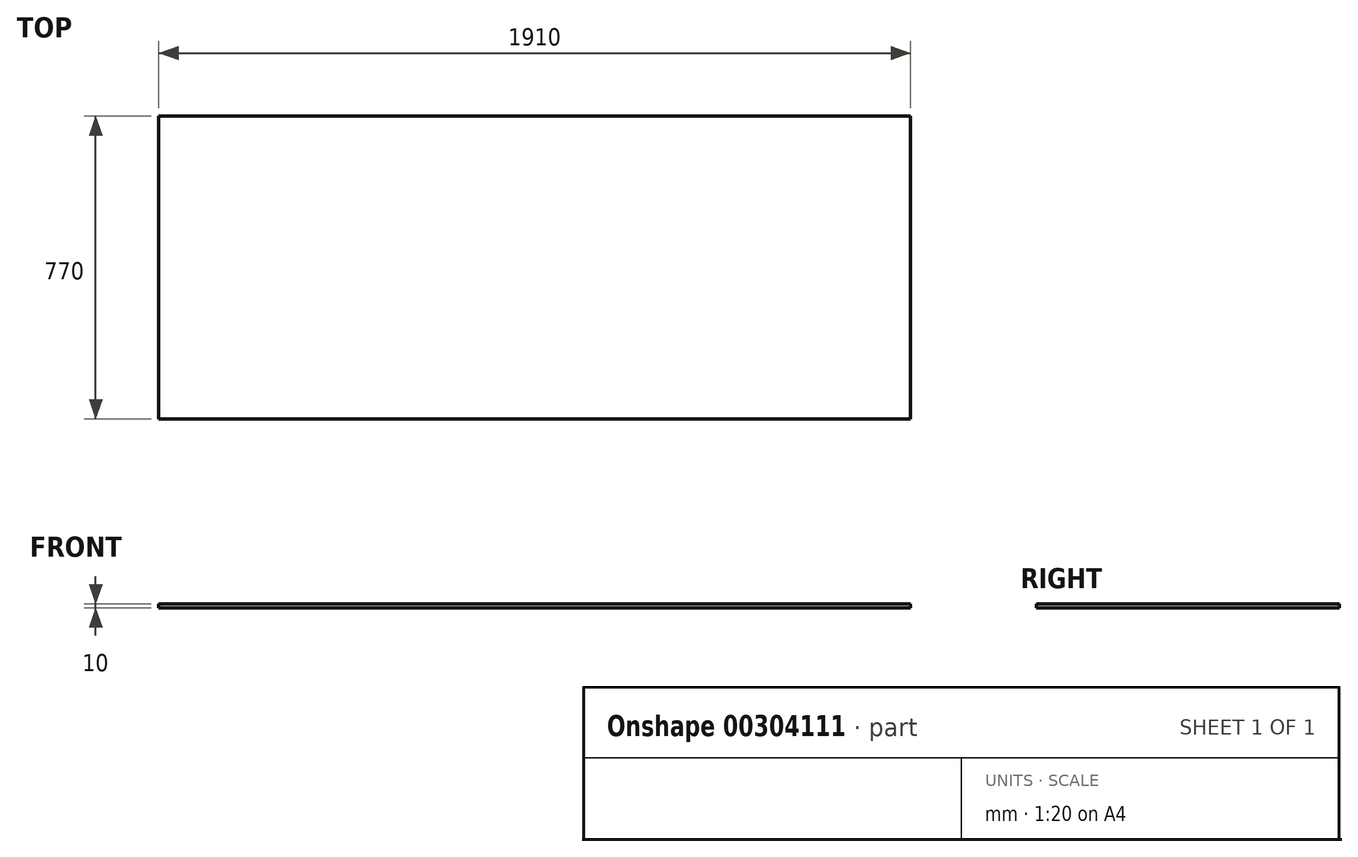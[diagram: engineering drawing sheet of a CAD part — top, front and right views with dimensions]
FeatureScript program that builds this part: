
annotation { "Feature Type Name" : "Feature", "Feature Type Description" : "" }
export const myFeature = defineFeature(function(context is Context, id is Id, definition is map)
    precondition{}
    {
        {
            var Q0;
            Q0=qCreatedBy(makeId("Top.planeOp"),FACE);
            var sketch = newSketch(context, id + "F0", { "sketchPlane" : qUnion([Q0])});
            skLineSegment(sketch, "E0.bottom", {"start": v(-946.22, 241.09) * mm, "end": v(963.78, 241.09) * mm});
            skLineSegment(sketch, "E0.top", {"start": v(-946.22, -528.91) * mm, "end": v(963.78, -528.91) * mm});
            skLineSegment(sketch, "E0.left", {"start": v(-946.22, 241.09) * mm, "end": v(-946.22, -528.91) * mm});
            skLineSegment(sketch, "E0.right", {"start": v(963.78, 241.09) * mm, "end": v(963.78, -528.91) * mm});
            skSolve(sketch);
        }
        {
            var Q0;
            Q0=makeQuery(id+"F0.imprint","IMPRINT",FACE,{"disambiguationData":[TD([[makeQuery(id+"F0.imprint","IMPRINT",EDGE,{"derivedFrom":sQuery(id+"F0.wireOp",EDGE,"E0.bottom")}),-1.0]])]});
            extrude(context, id + "F1", {"entities" : qUnion([Q0]), "depth" : 10 * mm, "offsetDistance" : 25 * mm});
        }
    });
